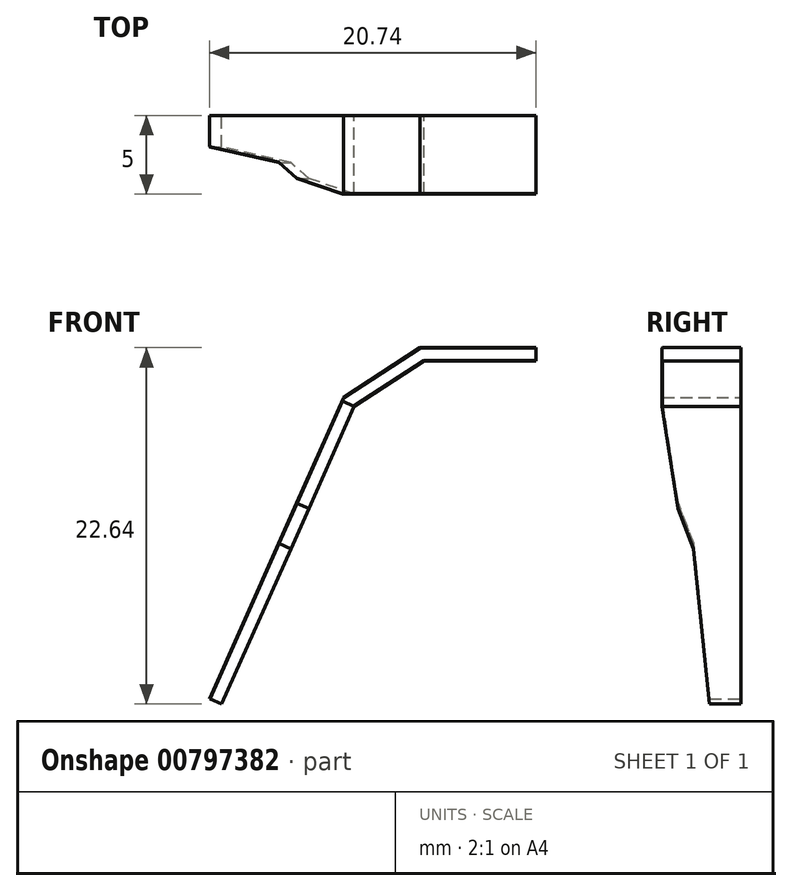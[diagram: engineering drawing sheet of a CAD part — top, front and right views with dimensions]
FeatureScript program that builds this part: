
annotation { "Feature Type Name" : "Feature", "Feature Type Description" : "" }
export const myFeature = defineFeature(function(context is Context, id is Id, definition is map)
    precondition{}
    {
        {
            var Q0;
            Q0=qCreatedBy(makeId("Front.planeOp"),FACE);
            var sketch = newSketch(context, id + "F0", { "sketchPlane" : qUnion([Q0])});
            skLineSegment(sketch, "E0", {"start": v(0, 0) * mm, "end": v(-7.11, 0) * mm});
            skLineSegment(sketch, "E1", {"start": v(-7.11, 0) * mm, "end": v(-11.55, -2.88) * mm});
            skLineSegment(sketch, "E2", {"start": v(-11.55, -2.88) * mm, "end": v(-19.97, -21.8) * mm});
            skLineSegment(sketch, "E3.0", {"start": v(-12.22, -2.3) * mm, "end": v(-20.74, -21.45) * mm});
            skLineSegment(sketch, "E3.1", {"start": v(-7.36, 0.85) * mm, "end": v(-12.22, -2.3) * mm});
            skLineSegment(sketch, "E3.2", {"start": v(0, 0.85) * mm, "end": v(-7.36, 0.85) * mm});
            skLineSegment(sketch, "E4", {"start": v(0, 0.85) * mm, "end": v(0, 0) * mm});
            skLineSegment(sketch, "E5", {"start": v(-20.74, -21.45) * mm, "end": v(-19.97, -21.8) * mm});
            skSolve(sketch);
        }
        {
            var Q0;
            Q0=makeQuery(id+"F0.imprint","IMPRINT",FACE,{"disambiguationData":[TD([[makeQuery(id+"F0.imprint","IMPRINT",EDGE,{"derivedFrom":sQuery(id+"F0.wireOp",EDGE,"E0")}),-1.0]])]});
            extrude(context, id + "F1", {"entities" : qUnion([Q0]), "depth" : 5 * mm, "offsetDistance" : 25 * mm});
        }
        {
            var Q0;
            Q0=makeQuery(id+"F1.opExtrude","SWEPT_FACE",FACE,{"disambiguationData":[OSD([sQuery(id+"F0.wireOp",EDGE,"E2")])]});
            var sketch = newSketch(context, id + "F2", { "sketchPlane" : qUnion([Q0])});
            skLineSegment(sketch, "E6", {"start": v(0, -7.33) * mm, "end": v(0, -14.43) * mm});
            skLineSegment(sketch, "E7", {"start": v(0, -14.43) * mm, "end": v(-4, -14.43) * mm});
            skLineSegment(sketch, "E8", {"start": v(0, -14.43) * mm, "end": v(0, -17.23) * mm});
            skLineSegment(sketch, "E9", {"start": v(0, -17.23) * mm, "end": v(-3, -17.23) * mm});
            skLineSegment(sketch, "E10", {"start": v(0, -17.23) * mm, "end": v(0, -28.03) * mm});
            skLineSegment(sketch, "E11", {"start": v(0, -28.03) * mm, "end": v(-2, -28.03) * mm});
            skLineSegment(sketch, "E12", {"start": v(-5, -7.33) * mm, "end": v(-4, -14.43) * mm});
            skLineSegment(sketch, "E13", {"start": v(-4, -14.43) * mm, "end": v(-3, -17.23) * mm});
            skLineSegment(sketch, "E14", {"start": v(-3, -17.23) * mm, "end": v(-2, -28.03) * mm});
            skLineSegment(sketch, "E15", {"start": v(-2, -28.03) * mm, "end": v(-5, -28.03) * mm});
            skLineSegment(sketch, "E16", {"start": v(-5, -28.03) * mm, "end": v(-5, -7.33) * mm});
            skSolve(sketch);
        }
        {
            var Q0;
            Q0=makeQuery(id+"F2.imprint","IMPRINT",FACE,{"disambiguationData":[TD([[makeQuery(id+"F2.imprint","IMPRINT",EDGE,{"derivedFrom":sQuery(id+"F2.wireOp",EDGE,"E12")}),-1.0]])]});
            extrude(context, id + "F3", {"entities" : qUnion([Q0]), "operationType" : NewBodyOperationType.REMOVE, "oppositeDirection" : true, "depth" : 25 * mm, "offsetDistance" : 25 * mm});
        }
        {
            var Q0;
            Q0=makeQuery(id+"F3.boolean.opBoolean","COPY",EDGE,{"derivedFrom":makeQuery(id+"F3.opExtrude","CAP_EDGE",EDGE,{"disambiguationData":[OSD([sQuery(id+"F2.wireOp",EDGE,"E14")])],"isStart":true})});
            var Q1;
            Q1=makeQuery(id+"F3.boolean.opBoolean","COPY",EDGE,{"derivedFrom":makeQuery(id+"F3.opExtrude","CAP_EDGE",EDGE,{"disambiguationData":[OSD([sQuery(id+"F2.wireOp",EDGE,"E13")])],"isStart":true})});
            var Q2;
            Q2=makeQuery(id+"F1.opExtrude","CAP_EDGE",EDGE,{"disambiguationData":[OSD([sQuery(id+"F0.wireOp",EDGE,"E0")])],"isStart":false});
            var Q3;
            Q3=makeQuery(id+"F1.opExtrude","CAP_EDGE",EDGE,{"disambiguationData":[OSD([sQuery(id+"F0.wireOp",EDGE,"E1")])],"isStart":false});
            var Q4;
            Q4=makeQuery(id+"F1.opExtrude","CAP_EDGE",EDGE,{"disambiguationData":[OSD([sQuery(id+"F0.wireOp",EDGE,"E3.1")])],"isStart":false});
            chamfer(context, id + "F4", {"entities" : qUnion([Q0, Q1, Q2, Q3, Q4]), "width" : 0.03 * mm, "tangentPropagation" : true});
        }
        {
            var Q0;
            Q0=makeQuery(id+"F3.boolean.opBoolean","COPY",EDGE,{"derivedFrom":makeQuery(id+"F3.opExtrude","CAP_EDGE",EDGE,{"disambiguationData":[OSD([sQuery(id+"F2.wireOp",EDGE,"E12")])],"isStart":true})});
            var Q1;
            Q1=makeQuery(id+"F3.boolean.opBoolean","INTERSECT",EDGE,{"derivedFrom":[makeQuery(id+"F1.opExtrude","SWEPT_FACE",FACE,{"disambiguationData":[OSD([sQuery(id+"F0.wireOp",EDGE,"E3.0")])]}),makeQuery(id+"F3.opExtrude","SWEPT_FACE",FACE,{"disambiguationData":[OSD([sQuery(id+"F2.wireOp",EDGE,"E12")])]})]});
            var Q2;
            Q2=makeQuery(id+"F1.opExtrude","CAP_EDGE",EDGE,{"disambiguationData":[OSD([sQuery(id+"F0.wireOp",EDGE,"E3.2")])],"isStart":false});
            var Q3;
            Q3=makeQuery(id+"F3.boolean.opBoolean","INTERSECT",EDGE,{"derivedFrom":[makeQuery(id+"F1.opExtrude","SWEPT_FACE",FACE,{"disambiguationData":[OSD([sQuery(id+"F0.wireOp",EDGE,"E3.0")])]}),makeQuery(id+"F3.opExtrude","SWEPT_FACE",FACE,{"disambiguationData":[OSD([sQuery(id+"F2.wireOp",EDGE,"E13")])]})]});
            var Q4;
            Q4=makeQuery(id+"F3.boolean.opBoolean","INTERSECT",EDGE,{"derivedFrom":[makeQuery(id+"F1.opExtrude","SWEPT_FACE",FACE,{"disambiguationData":[OSD([sQuery(id+"F0.wireOp",EDGE,"E3.0")])]}),makeQuery(id+"F3.opExtrude","SWEPT_FACE",FACE,{"disambiguationData":[OSD([sQuery(id+"F2.wireOp",EDGE,"E14")])]})]});
            chamfer(context, id + "F5", {"entities" : qUnion([Q0, Q1, Q2, Q3, Q4]), "width" : 0.03 * mm, "tangentPropagation" : true});
        }
    });
